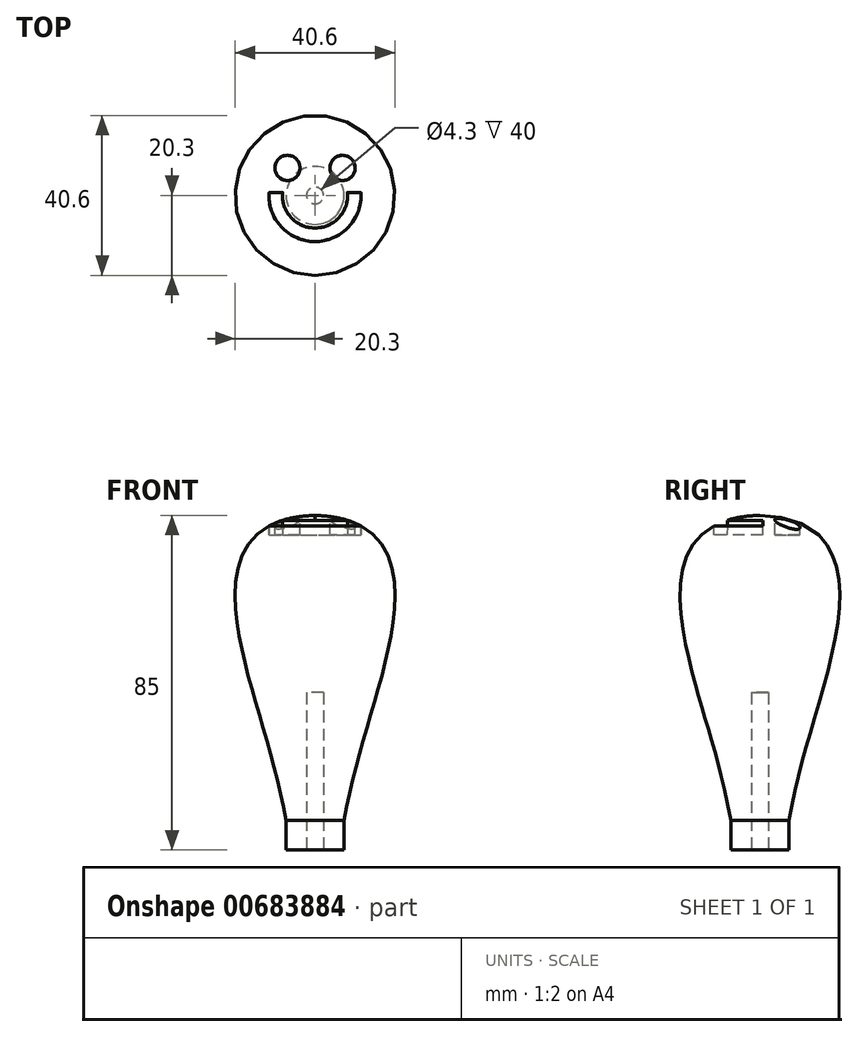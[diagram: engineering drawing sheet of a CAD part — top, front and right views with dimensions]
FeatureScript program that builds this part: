
annotation { "Feature Type Name" : "Feature", "Feature Type Description" : "" }
export const myFeature = defineFeature(function(context is Context, id is Id, definition is map)
    precondition{}
    {
        {
            var Q0;
            Q0=qCreatedBy(makeId("Top.planeOp"),FACE);
            var sketch = newSketch(context, id + "F0", { "sketchPlane" : qUnion([Q0])});
            skCircle(sketch, "E0", {"center": v(0, 0) * mm, "radius": 2.15 * mm});
            skSolve(sketch);
        }
        {
            var Q0;
            Q0=qCreatedBy(makeId("Right.planeOp"),FACE);
            var sketch = newSketch(context, id + "F1", { "sketchPlane" : qUnion([Q0])});
            skLineSegment(sketch, "E1", {"start": v(0, 0) * mm, "end": v(-6, 0) * mm});
            skFitSpline(sketch, "E2", {"points": [v(-6, 0) * mm, v(-17.58, 46.74) * mm, v(0, 85) * mm], "startDerivative": vector(-23.17, 138.15) * mm, "endDerivative": vector(156.65, 3.57) * mm});
            skLineSegment(sketch, "E3", {"start": v(0, 85) * mm, "end": v(0, 0) * mm});
            skSolve(sketch);
        }
        {
            var Q0;
            Q0=makeQuery(id+"F1.imprint","IMPRINT",FACE,{"disambiguationData":[TD([[makeQuery(id+"F1.imprint","IMPRINT",EDGE,{"derivedFrom":sQuery(id+"F1.wireOp",EDGE,"E1")}),-1.0]])]});
            var Q1;
            Q1=sQuery(id+"F1.wireOp",EDGE,"E3");
            revolve(context, id + "F2", {"entities" : qUnion([Q0]), "axis" : qUnion([Q1]), "revolveType" : RevolveType.FULL});
        }
        {
            var Q0;
            Q0 = qSketchRegion(id + "F0", true);
            extrude(context, id + "F3", {"entities" : qUnion([Q0]), "operationType" : NewBodyOperationType.REMOVE, "depth" : 40 * mm, "offsetDistance" : 25 * mm});
        }
        {
            var Q0;
            Q0=qCreatedBy(makeId("Top.planeOp"),FACE);
            var sketch = newSketch(context, id + "F4", { "sketchPlane" : qUnion([Q0])});
            skCircle(sketch, "E4", {"center": v(0, 0) * mm, "radius": 4.74 * mm});
            skCircle(sketch, "E5", {"center": v(0, 0) * mm, "radius": 7.36 * mm});
            skSolve(sketch);
        }
        {
            var Q0;
            Q0=makeQuery(id+"F4.imprint","IMPRINT",FACE,{"disambiguationData":[TD([[makeQuery(id+"F4.imprint","IMPRINT",EDGE,{"derivedFrom":sQuery(id+"F4.wireOp",EDGE,"E4")}),-1.0]])]});
            extrude(context, id + "F5", {"entities" : qUnion([Q0]), "operationType" : NewBodyOperationType.ADD, "depth" : 25 * mm, "offsetDistance" : 25 * mm});
        }
        {
            var Q0;
            Q0=qCreatedBy(makeId("Top.planeOp"),FACE);
            var sketch = newSketch(context, id + "F6", { "sketchPlane" : qUnion([Q0])});
            skArc(sketch, "E6", {"start": v(-11, 0) * mm, "mid": v(0, -11) * mm, "end": v(11, 0) * mm});
            skArc(sketch, "E7.0", {"start": v(-9, 0) * mm, "mid": v(0, -9) * mm, "end": v(9, 0) * mm});
            skLineSegment(sketch, "E8", {"start": v(-11, 0) * mm, "end": v(-9, 0) * mm});
            skLineSegment(sketch, "E9", {"start": v(11, 0) * mm, "end": v(9, 0) * mm});
            skLineSegment(sketch, "E10", {"start": v(0, 0) * mm, "end": v(0, 7) * mm, "construction": true});
            skLineSegment(sketch, "E11", {"start": v(0, 7) * mm, "end": v(-7, 7) * mm, "construction": true});
            skLineSegment(sketch, "E12", {"start": v(-7, 7) * mm, "end": v(-7, 11) * mm, "construction": true});
            skLineSegment(sketch, "E13", {"start": v(-7, 11) * mm, "end": v(7, 11) * mm, "construction": true});
            skLineSegment(sketch, "E14", {"start": v(7, 11) * mm, "end": v(7, 7) * mm, "construction": true});
            skCircle(sketch, "E15", {"center": v(-7, 7) * mm, "radius": 2.5 * mm});
            skCircle(sketch, "E16", {"center": v(7, 7) * mm, "radius": 2.5 * mm});
            skSolve(sketch);
        }
        {
            var Q0;
            Q0 = qSketchRegion(id + "F6", true);
            extrude(context, id + "F7", {"entities" : qUnion([Q0]), "operationType" : NewBodyOperationType.REMOVE, "depth" : 100 * mm, "offsetDistance" : 25 * mm, "hasDraft" : true, "draftAngle" : .5 * degree, "hasSecondDirection" : true, "secondDirectionOppositeDirection" : false, "secondDirectionDepth" : 80 * mm});
        }
    });
